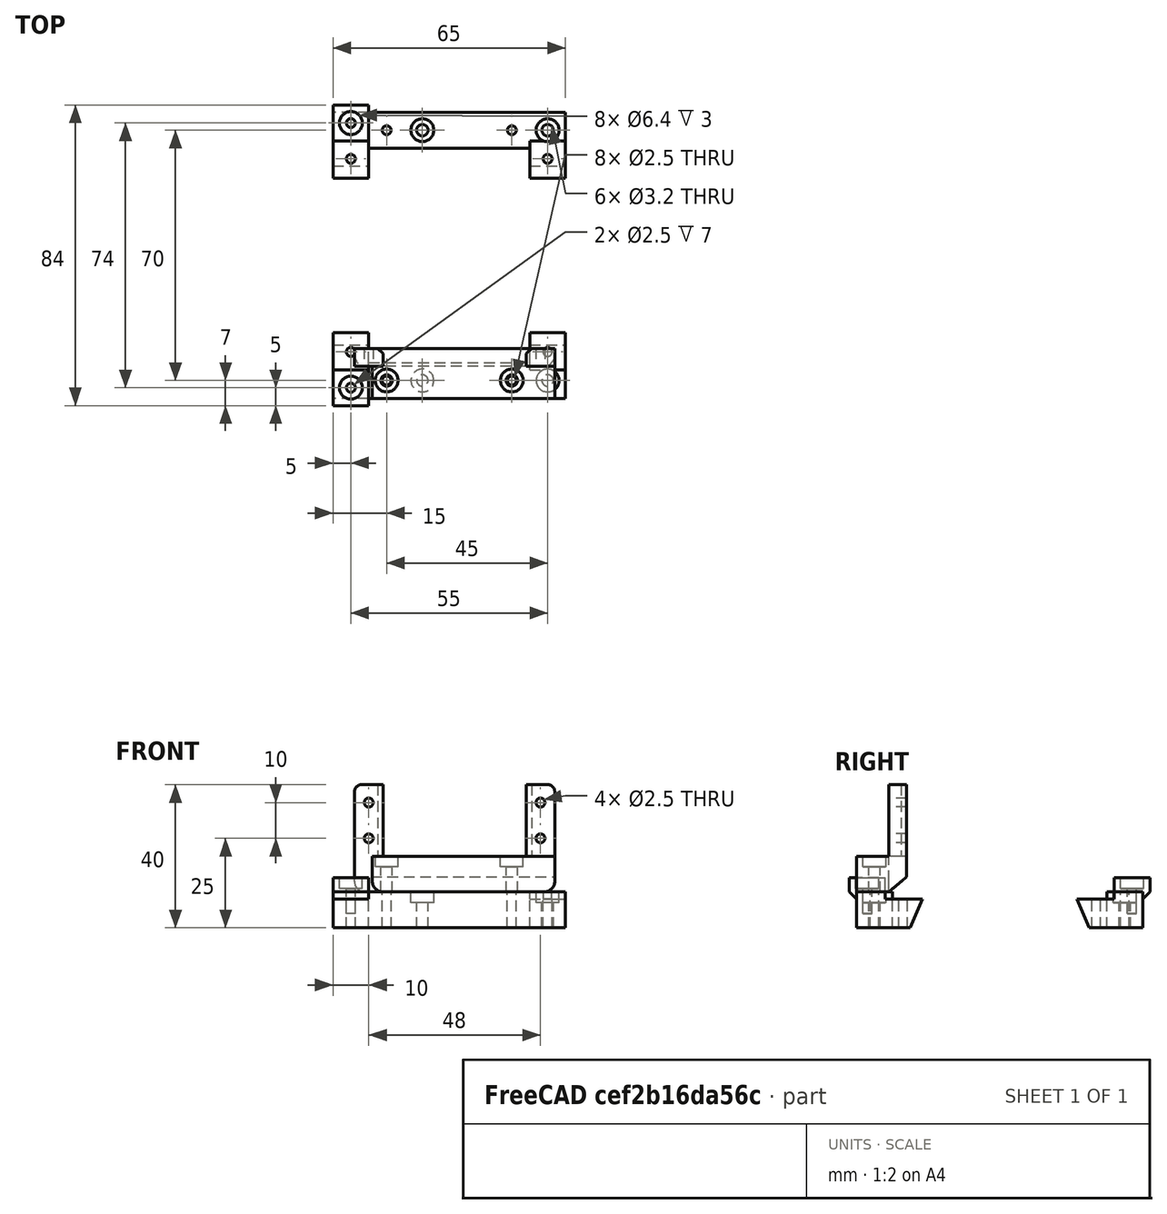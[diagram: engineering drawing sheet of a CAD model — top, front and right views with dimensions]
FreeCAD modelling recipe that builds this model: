
FCSTD DOCUMENT  (FreeCAD 0.16R5958 (Git))
Label: gearbox-holder-01
License: CC-BY 3.0
LicenseURL: http://creativecommons.org/licenses/by/3.0/
objects: Part::MultiFuse×36, Part::Box×29, Part::Cylinder×26, Part::Cut×18, Part::Fillet×9, Part::Chamfer×4, Part::Mirroring×2
note: 124 computed .brp shape members not serialized (recipe doc carries the construction recipe); baked Part::Feature solids carry a one-line shape summary decoded from their .brp

FEATURE [Part::Box] Box  label="Cube"
  Height = 10
  Length = 65
  Width = 80
FEATURE [Part::Box] Box001  label="Cube001"
  Height = 10
  Length = 65
  Placement = pos=(0,19,0) rot=(0,0,1;0rad)
  Width = 42
FEATURE [Part::Cylinder] Cylinder
  Angle = 360
  Height = 10
  Radius = 1.25
FEATURE [Part::Cylinder] Cylinder001
  Angle = 360
  Height = 10
  Placement = pos=(0,54,0) rot=(0,0,1;0rad)
  Radius = 1.25
FEATURE [Part::MultiFuse] Fusion
  Placement = pos=(5,13,0) rot=(0,0,1;0rad)
  Shapes = -> [Cylinder,Cylinder001]
FEATURE [Part::Cylinder] Cylinder002
  Angle = 360
  Height = 10
  Placement = pos=(0,54,0) rot=(0,0,1;0rad)
  Radius = 1.25
FEATURE [Part::Cylinder] Cylinder003
  Angle = 360
  Height = 10
  Radius = 1.25
FEATURE [Part::MultiFuse] Fusion001
  Placement = pos=(60,13,0) rot=(0,0,1;0rad)
  Shapes = -> [Cylinder003,Cylinder002]
FEATURE [Part::MultiFuse] Fusion002
  Shapes = -> [Fusion,Fusion001]
FEATURE [Part::Cylinder] Cylinder004
  Angle = 360
  Height = 10
  Placement = pos=(5,0,0) rot=(0,0,1;0rad)
  Radius = 1.6
FEATURE [Part::Cylinder] Cylinder005
  Angle = 360
  Height = 10
  Placement = pos=(5,70,0) rot=(0,0,1;0rad)
  Radius = 1.6
FEATURE [Part::MultiFuse] Fusion003
  Placement = pos=(0,5,0) rot=(0,0,1;0rad)
  Shapes = -> [Cylinder005,Cylinder004]
FEATURE [Part::Cylinder] Cylinder006
  Angle = 360
  Height = 3
  Placement = pos=(5,70,0) rot=(0,0,1;0rad)
  Radius = 3.2
FEATURE [Part::Cylinder] Cylinder007
  Angle = 360
  Height = 3
  Placement = pos=(5,0,0) rot=(0,0,1;0rad)
  Radius = 3.2
FEATURE [Part::MultiFuse] Fusion004
  Placement = pos=(0,5,7) rot=(0,0,1;0rad)
  Shapes = -> [Cylinder006,Cylinder007]
FEATURE [Part::MultiFuse] Fusion005
  Placement = pos=(55,0,0) rot=(0,0,1;0rad)
  Shapes = -> [Fusion003,Fusion004]
FEATURE [Part::MultiFuse] Fusion006
  Placement = pos=(0,5,7) rot=(0,0,1;0rad)
  Shapes = -> [Cylinder006,Cylinder007]
FEATURE [Part::MultiFuse] Fusion008
  Placement = pos=(0,5,0) rot=(0,0,1;0rad)
  Shapes = -> [Cylinder005,Cylinder004]
FEATURE [Part::MultiFuse] Fusion007
  Placement = pos=(20,0,0) rot=(0,0,1;0rad)
  Shapes = -> [Fusion008,Fusion006]
FEATURE [Part::MultiFuse] Fusion009
  Shapes = -> [Fusion005,Fusion007]
FEATURE [Part::Cylinder] Cylinder010
  Angle = 360
  Height = 10
  Placement = pos=(0,70,0) rot=(0,0,1;0rad)
  Radius = 1.25
FEATURE [Part::Cylinder] Cylinder011
  Angle = 360
  Height = 10
  Radius = 1.25
FEATURE [Part::Box] Box002  label="Cube002"
  Height = 10
  Length = 10
  Placement = pos=(0,-2,4) rot=(0,0,1;0rad)
  Width = 10
FEATURE [Part::Chamfer] Chamfer002
  Base = -> Box002
  Edges = 1 edges r=6: [Edge9]
FEATURE [Part::Cut] Cut
  Base = -> Box
  Tool = -> Box001
FEATURE [Part::Box] Box003
  Height = 10
  Length = 45
  Placement = pos=(10,10,0) rot=(0,0,1;0rad)
  Width = 9
FEATURE [Part::Box] Box004
  Height = 10
  Length = 45
  Placement = pos=(10,61,0) rot=(0,0,1;0rad)
  Width = 9
FEATURE [Part::MultiFuse] Fusion010
  Shapes = -> [Box003,Box004]
FEATURE [Part::Cut] Cut006
  Base = -> Cut
  Tool = -> Fusion010
FEATURE [Part::Cut] Cut007
  Base = -> Cut006
  Tool = -> Fusion002
FEATURE [Part::MultiFuse] Fusion011
  Placement = pos=(50,5,0) rot=(0,0,1;0rad)
  Shapes = -> [Cylinder010,Cylinder011]
FEATURE [Part::Cylinder] Cylinder014
  Angle = 360
  Height = 10
  Radius = 1.25
FEATURE [Part::Cylinder] Cylinder015
  Angle = 360
  Height = 10
  Placement = pos=(0,70,0) rot=(0,0,1;0rad)
  Radius = 1.25
FEATURE [Part::MultiFuse] Fusion012
  Placement = pos=(15,5,0) rot=(0,0,1;0rad)
  Shapes = -> [Cylinder015,Cylinder014]
FEATURE [Part::Box] Box005
  Height = 12
  Length = 65
  Placement = pos=(0,15,0) rot=(-1,0,0;0.401426rad)
  Width = 10
FEATURE [Part::Mirroring] Part__Mirroring  label="Box005 (Mirror #1)"
  Base = (0,0,0)
  Normal = (0,1,0)
  Placement = pos=(0,80,0) rot=(0,0,1;0rad)
  Source = -> Box005
FEATURE [Part::Box] Box006
  Height = 12
  Length = 65
  Placement = pos=(0,15,0) rot=(-1,0,0;0.401426rad)
  Width = 10
FEATURE [Part::MultiFuse] Fusion013
  Shapes = -> [Part__Mirroring,Box006]
FEATURE [Part::Cut] Cut008
  Base = -> Cut007
  Tool = -> Fusion013
FEATURE [Part::MultiFuse] Fusion014
  Shapes = -> [Fusion009,Fusion011,Fusion012]
FEATURE [Part::Cut] Cut009
  Base = -> Cut008
  Tool = -> Fusion014
FEATURE [Part::Box] Box007  label="Cube003"
  Height = 10
  Length = 10
  Placement = pos=(0,-2,4) rot=(0,0,1;0rad)
  Width = 10
FEATURE [Part::Chamfer] Chamfer
  Base = -> Box007
  Edges = 1 edges r=6: [Edge9]
FEATURE [Part::Mirroring] Part__Mirroring001  label="Chamfer (Mirror #2)"
  Base = (0,0,0)
  Normal = (0,1,0)
  Placement = pos=(0,80,0) rot=(0,0,1;0rad)
  Source = -> Chamfer
FEATURE [Part::MultiFuse] Fusion015
  Shapes = -> [Chamfer002,Cut009,Part__Mirroring001]
FEATURE [Part::Cylinder] Cylinder016
  Angle = 360
  Height = 10
  Placement = pos=(5,3,4) rot=(0,0,1;0rad)
  Radius = 1.25
FEATURE [Part::Cylinder] Cylinder017
  Angle = 360
  Height = 3
  Placement = pos=(5,3,11) rot=(0,0,1;0rad)
  Radius = 3.2
FEATURE [Part::MultiFuse] Fusion016
  Shapes = -> [Cylinder016,Cylinder017]
FEATURE [Part::Cylinder] Cylinder018
  Angle = 360
  Height = 3
  Placement = pos=(5,3,11) rot=(0,0,1;0rad)
  Radius = 3.2
FEATURE [Part::Cylinder] Cylinder019
  Angle = 360
  Height = 10
  Placement = pos=(5,3,4) rot=(0,0,1;0rad)
  Radius = 1.25
FEATURE [Part::MultiFuse] Fusion017
  Placement = pos=(0,74,0) rot=(0,0,1;0rad)
  Shapes = -> [Cylinder019,Cylinder018]
FEATURE [Part::MultiFuse] Fusion018
  Shapes = -> [Fusion016,Fusion017]
FEATURE [Part::Cut] Cut010
  Base = -> Fusion015
  Tool = -> Fusion018
FEATURE [Part::Box] Box008
  Height = 2
  Length = 10
  Placement = pos=(0,8,8) rot=(0,0,1;0rad)
  Width = 11
FEATURE [Part::Box] Box009
  Height = 2
  Length = 10
  Placement = pos=(0,61,8) rot=(0,0,1;0rad)
  Width = 11
FEATURE [Part::Box] Box010
  Height = 2
  Length = 10
  Placement = pos=(55,8,8) rot=(0,0,1;0rad)
  Width = 11
FEATURE [Part::Box] Box011
  Height = 2
  Length = 10
  Placement = pos=(55,61,8) rot=(0,0,1;0rad)
  Width = 11
FEATURE [Part::MultiFuse] Fusion019
  Shapes = -> [Box008,Box010,Box011,Box009]
FEATURE [Part::Cut] Cut011  label="gearbox-holder"
  Base = -> Cut010
  Tool = -> Fusion019
FEATURE [Part::Box] Box012
  Height = 5
  Length = 56
  Placement = pos=(-14,1,0) rot=(0,0,1;0rad)
  Width = 10
FEATURE [Part::Cut] Cut012
  Placement = pos=(-18,19,0) rot=(0,0,1;0rad)
FEATURE [Part::Fillet] Fillet
  Base = -> Cut012
  Edges = 1 edges r=0.6: [Edge14]
  Placement = pos=(29,0,0) rot=(0,0,1;0rad)
FEATURE [Part::Box] Box013
  Height = 10
  Length = 17
  Placement = pos=(20,22,0) rot=(0,0,1;0rad)
  Width = 10
FEATURE [Part::Box] Box014
  Height = 10
  Length = 9
  Placement = pos=(20,11,0) rot=(0,0,1;0rad)
  Width = 21
FEATURE [Part::MultiFuse] Fusion020
  Shapes = -> [Box013,Box014]
FEATURE [Part::Cut] Cut013
  Base = -> Fillet
  Tool = -> Fusion020
FEATURE [Part::Box] Box015
  Height = 3.4
  Length = 21
  Placement = pos=(8,11,0) rot=(0,0,1;0rad)
  Width = 5
FEATURE [Part::MultiFuse] Fusion021
  Shapes = -> [Box012,Cut013,Box015]
FEATURE [Part::Box] Box016
  Height = 5
  Length = 8
  Placement = pos=(34,-19,0) rot=(0,0,1;0rad)
  Width = 20
FEATURE [Part::Box] Box017
  Height = 5
  Length = 8
  Placement = pos=(-14,-19,0) rot=(0,0,1;0rad)
  Width = 20
FEATURE [Part::Cylinder] Cylinder020
  Angle = 360
  Height = 10
  Placement = pos=(-10,0,0) rot=(0,0,1;0rad)
  Radius = 1.25
FEATURE [Part::Cylinder] Cylinder021
  Angle = 360
  Height = 10
  Placement = pos=(-10,-10,0) rot=(0,0,1;0rad)
  Radius = 1.25
FEATURE [Part::MultiFuse] Fusion022
  Placement = pos=(0,-4,0) rot=(0,0,1;0rad)
  Shapes = -> [Cylinder021,Cylinder020]
FEATURE [Part::Cylinder] Cylinder022
  Angle = 360
  Height = 10
  Placement = pos=(-10,0,0) rot=(0,0,1;0rad)
  Radius = 1.25
FEATURE [Part::Cylinder] Cylinder023
  Angle = 360
  Height = 10
  Placement = pos=(-10,-10,0) rot=(0,0,1;0rad)
  Radius = 1.25
FEATURE [Part::MultiFuse] Fusion023
  Placement = pos=(48,-4,0) rot=(0,0,1;0rad)
  Shapes = -> [Cylinder023,Cylinder022]
FEATURE [Part::Box] Box018
  Height = 3.4
  Length = 17
  Placement = pos=(-9,11,0) rot=(0,0,1;0rad)
  Width = 15
FEATURE [Part::MultiFuse] Fusion024
  Shapes = -> [Fusion022,Fusion023]
FEATURE [Part::Cylinder] Cylinder024
  Angle = 360
  Height = 10
  Placement = pos=(5,19,0) rot=(0,0,1;0rad)
  Radius = 1.6
FEATURE [Part::Cylinder] Cylinder025
  Angle = 360
  Height = 10
  Placement = pos=(-6,19,0) rot=(0,0,1;0rad)
  Radius = 1.6
FEATURE [Part::MultiFuse] Fusion025
  Shapes = -> [Cylinder024,Cylinder025]
FEATURE [Part::Cut] Cut014
  Base = -> Box018
  Tool = -> Fusion025
FEATURE [Part::MultiFuse] Fusion026
  Shapes = -> [Box016,Box017,Cut014,Fusion021]
FEATURE [Part::Cut] Cut015
  Base = -> Fusion026
  Tool = -> Fusion024
FEATURE [Part::Fillet] Fillet001
  Base = -> Cut015
  Edges = 6 edges r=2: [Edge51,Edge54,Edge56,Edge58,Edge59,Edge61]
FEATURE [Part::Fillet] Fillet002
  Base = -> Fillet001
  Edges = 1 edges r=1.5: [Edge36]
FEATURE [Part::Fillet] Fillet003
  Base = -> Fillet002
  Edges = 2 edges r=3: [Edge30,Edge33]
FEATURE [Part::Box] Box019
  Height = 1.6
  Length = 19
  Placement = pos=(-10,10,3.4) rot=(0,0,1;0rad)
  Width = 10
FEATURE [Part::Cut] Cut016
  Base = -> Fillet003
  Tool = -> Box019
FEATURE [Part::Fillet] Fillet004
  Base = -> Cut016
  Edges = 2 edges r=2: [Edge42,Edge63]
FEATURE [Part::Box] Box020
  Height = 1
  Length = 4
  Placement = pos=(-2.5,25,0) rot=(0,0,1;0rad)
  Width = 1
FEATURE [Part::Cut] Cut017
  Base = -> Fillet004
  Tool = -> Box020
FEATURE [Part::Fillet] Fillet005
  Base = -> Cut017
  Edges = 1 edges r=0.99: [Edge94]
FEATURE [Part::Chamfer] Chamfer003
  Base = -> Fillet005
  Edges = 2 edges r=1.5: [Edge34,Edge36]
FEATURE [Part::MultiFuse] Fusion027
  Placement = pos=(48,-4,0) rot=(0,0,1;0rad)
  Shapes = -> [Cylinder023,Cylinder022]
FEATURE [Part::MultiFuse] Fusion029
  Placement = pos=(0,-4,0) rot=(0,0,1;0rad)
  Shapes = -> [Cylinder021,Cylinder020]
FEATURE [Part::MultiFuse] Fusion028
  Shapes = -> [Fusion029,Fusion027]
FEATURE [Part::Box] Box021
  Height = 5
  Length = 8
  Placement = pos=(34,-19,2) rot=(0,0,1;0rad)
  Width = 25
FEATURE [Part::Box] Box022
  Height = 5
  Length = 8
  Placement = pos=(-14,-19,2) rot=(0,0,1;0rad)
  Width = 25
FEATURE [Part::MultiFuse] Fusion030
  Shapes = -> [Box021,Box022]
FEATURE [Part::Cut] Cut018
  Base = -> Fusion030
  Tool = -> Fusion028
FEATURE [Part::Fillet] Fillet006
  Base = -> Cut018
  Edges = 2 edges r=2: [Edge6,Edge23]
FEATURE [Part::Chamfer] Chamfer004
  Base = -> Fillet006
  Edges = 2 edges r=2: [Edge18,Edge31]
FEATURE [Part::MultiFuse] Fusion031
  Placement = pos=(0,0,21) rot=(-1,0,0;1.5708rad)
  Shapes = -> [Chamfer003,Chamfer004]
FEATURE [Part::Box] Box023
  Height = 15
  Length = 53
  Placement = pos=(-13,0,-5) rot=(0,0,1;0rad)
  Width = 10
FEATURE [Part::Cut] Cut019
  Base = -> Fusion031
  Placement = pos=(0,0,0) rot=(0,0,1;3.14159rad)
  Tool = -> Box023
FEATURE [Part::Box] Box024
  Height = 1
  Length = 19
  Placement = pos=(-9,-5,10) rot=(0,0,1;0rad)
  Width = 5
FEATURE [Part::MultiFuse] Fusion032
  Placement = pos=(53,0,0) rot=(0,0,1;0rad)
  Shapes = -> [Cut019,Box024]
FEATURE [Part::Cylinder] Cylinder026
  Angle = 360
  Height = 10
  Placement = pos=(15,5,10) rot=(0,0,1;0rad)
  Radius = 1.6
FEATURE [Part::Cylinder] Cylinder027
  Angle = 360
  Height = 10
  Placement = pos=(50,5,10) rot=(0,0,1;0rad)
  Radius = 1.6
FEATURE [Part::Box] Box025
  Height = 10
  Length = 43
  Placement = pos=(11,0,10) rot=(0,0,1;0rad)
  Width = 10
FEATURE [Part::Fillet] Fillet007
  Base = -> Box025
  Edges = 1 edges r=3: [Edge4]
  Placement = pos=(0,-1,0) rot=(0,0,1;0rad)
FEATURE [Part::Cylinder] Cylinder028
  Angle = 360
  Height = 3
  Placement = pos=(15,5,17) rot=(0,0,1;0rad)
  Radius = 3.2
FEATURE [Part::Cylinder] Cylinder029
  Angle = 360
  Height = 3
  Placement = pos=(50,5,17) rot=(0,0,1;0rad)
  Radius = 3.2
FEATURE [Part::MultiFuse] Fusion034
  Shapes = -> [Cylinder026,Cylinder027,Cylinder028,Cylinder029]
FEATURE [Part::Box] Box026
  Height = 33
  Length = 56
  Placement = pos=(11,-15,10) rot=(0,0,1;0rad)
  Width = 10
FEATURE [Part::Box] Box027
  Height = 10
  Length = 13
  Placement = pos=(54,0,10) rot=(0,0,1;0rad)
  Width = 10
FEATURE [Part::Fillet] Fillet008
  Base = -> Box027
  Edges = 1 edges r=3: [Edge8]
  Placement = pos=(-5,-1,0) rot=(0,0,1;0rad)
FEATURE [Part::Cut] Cut020
  Base = -> Fusion032
  Placement = pos=(-5,14,0) rot=(0,0,1;0rad)
  Tool = -> Box026
FEATURE [Part::MultiFuse] Fusion035
  Placement = pos=(0,1,0) rot=(0,0,1;0rad)
  Shapes = -> [Fillet008,Fillet007]
FEATURE [Part::MultiFuse] Fusion036
  Shapes = -> [Cut020,Fusion035]
FEATURE [Part::Cut] Cut021
  Base = -> Fusion036
  Tool = -> Fusion034
FEATURE [Part::Box] Box028  label="Cube004"
  Height = 10
  Length = 56
  Placement = pos=(6,15,2) rot=(1,0,0;0.698132rad)
  Width = 10
FEATURE [Part::Cut] Cut022  label="steering-servo-holder"
  Base = -> Cut021
  Tool = -> Box028
